# Revit family: 357246xx0--Compact vitreous china wall-hung bidet - Meridian - Roca - 357246xx0
name_source: partatom
category: Plumbing Fixtures
units: mm (PartAtom-declared; Revit-internal decimal feet)

## family parameters
Always vertical = Yes
Cut with Voids When Loaded = No
Host = Wall
OmniClass Number = 23.45.00.00
OmniClass Title = Sanitary, Laundry, and Cleaning Equipment
Part Type = Normal
Room Calculation Point = No
Round Connector Dimension = Use Diameter
Shared = No

## types (2) — shared parameters
BIMobject category = Bidets
Depth = 360.00
Description = Compact vitreous china wall-hung bidet
Design country = Spain
Eco green certification = No
Edition number = 1
Height = 300 mm
IFC Classification = Furniture
Installation type = Wall-hung
Length = 480 mm  [stored 1.5748 ft]
Manufacturer name = Roca
Manufacturer url = http://www.roca.com
Model = 357246..0
NBS Reference Code = 35-06-11
NBS Reference Description = Bidets
Nominal height = 300.00
Nominal width = 480.00
Outlet Diameter = 46 mm  [stored 0.150919 ft]
Product data url = http://roca.bimobject.com
Product family = Meridian
Product group = Bidet
QR code = https://www.roca.com
Shape = Round
Suitable for Children = No
Suitable for Handicapped = No
Taphole configuration = 1 Taphole
Tapholes Diameter = 35 mm  [stored 0.114829 ft]
Technical description = http://www.roca.com
UNSPSC Code = 301815
UNSPSC Name = Sanitary ware
URL = http://www.roca.com
Uniclass 1.4 Code = L7215
Uniclass 1.4 Description = Bidets
Uniclass 2.0 Code = PR-35-06-11
Uniclass 2.0 Description = Bidets
Weight Net (Kg) = 0
Width = 360 mm  [stored 1.1811 ft]

## per-type parameters (varying)
| type | Product SKU |
| White - Meridian - Roca | A357246000 |
| Pergamon - Meridian - Roca | A357246170 |

note: column(s) folded — value = type name in every type: Material

note: [stored X ft] marks values corroborated as IEEE doubles in the binary element streams (Revit-internal decimal feet)

## geometry (parser evidence)
native form markers: Blend x2, Sweep x1
no freeform markers — native parametric forms only
